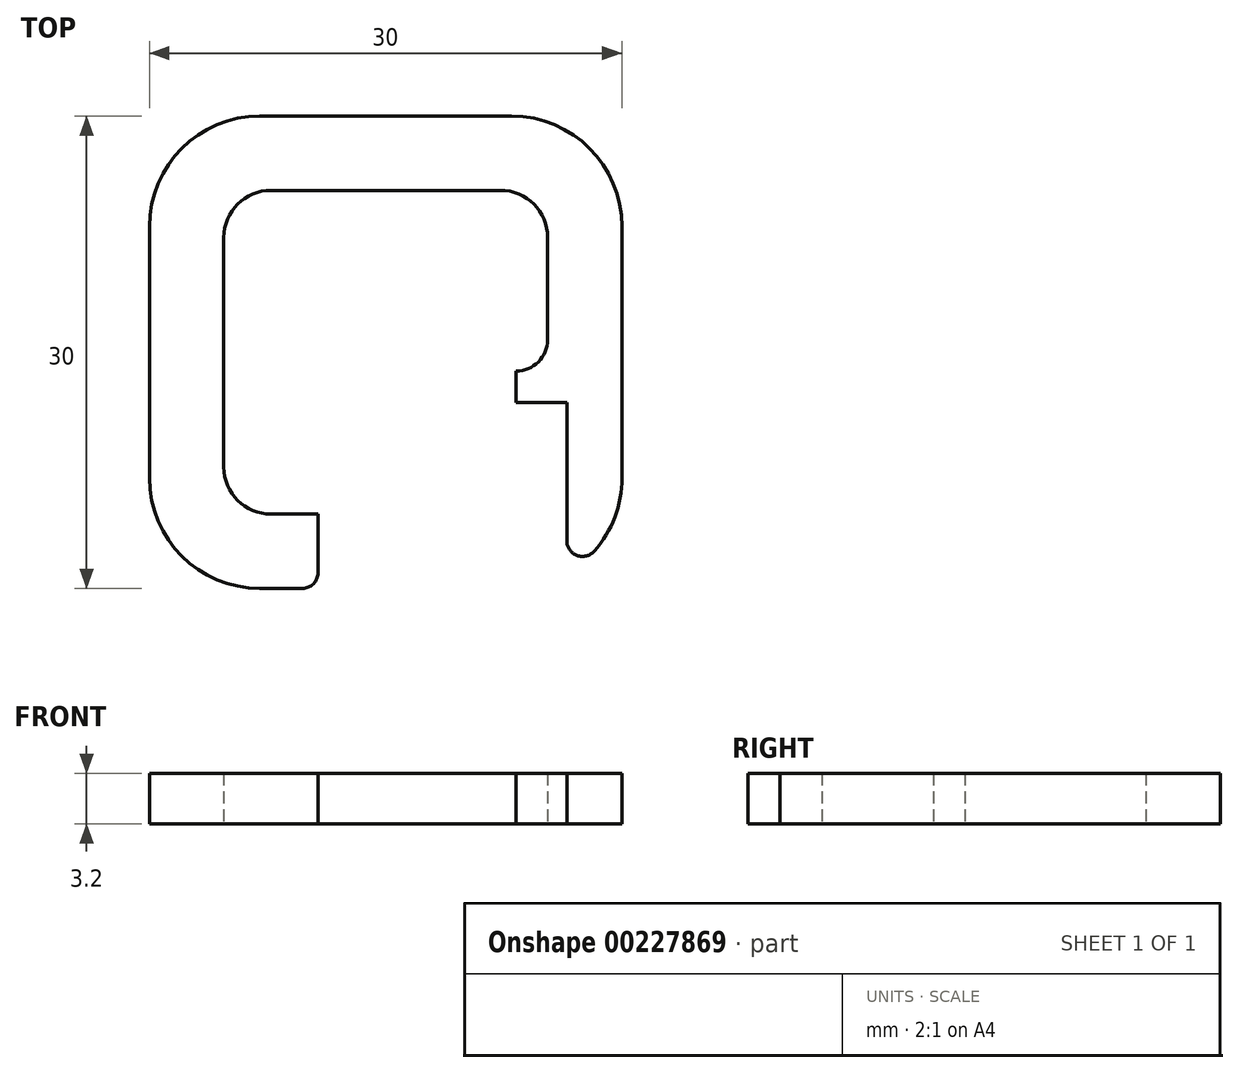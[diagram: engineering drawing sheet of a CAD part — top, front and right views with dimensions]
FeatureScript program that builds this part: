
annotation { "Feature Type Name" : "Feature", "Feature Type Description" : "" }
export const myFeature = defineFeature(function(context is Context, id is Id, definition is map)
    precondition{}
    {
        {
            var Q0;
            Q0=qCreatedBy(makeId("Top.planeOp"),FACE);
            var sketch = newSketch(context, id + "F0", { "sketchPlane" : qUnion([Q0])});
            skLineSegment(sketch, "E0.bottom", {"start": v(8, 15) * mm, "end": v(-8, 15) * mm});
            skLineSegment(sketch, "E0.left", {"start": v(15, 8) * mm, "end": v(15, -8) * mm});
            skLineSegment(sketch, "E0.right", {"start": v(-15, 8) * mm, "end": v(-15, -8) * mm});
            skPoint(sketch, "E1.visualSharp", {"position": v(-15, 15) * mm});
            skArc(sketch, "E1.filletArc", {"start": v(-8, 15) * mm, "mid": v(-12.95, 12.95) * mm, "end": v(-15, 8) * mm});
            skPoint(sketch, "E2.visualSharp", {"position": v(15, 15) * mm});
            skArc(sketch, "E2.filletArc", {"start": v(15, 8) * mm, "mid": v(12.95, 12.95) * mm, "end": v(8, 15) * mm});
            skPoint(sketch, "E3.visualSharp", {"position": v(15, -15) * mm});
            skArc(sketch, "E3.filletArc", {"start": v(13.25, -12.63) * mm, "mid": v(14.55, -10.47) * mm, "end": v(15, -8) * mm});
            skPoint(sketch, "E4.visualSharp", {"position": v(-15, -15) * mm});
            skArc(sketch, "E4.filletArc", {"start": v(-15, -8) * mm, "mid": v(-12.95, -12.95) * mm, "end": v(-8, -15) * mm});
            skLineSegment(sketch, "E5.left", {"start": v(-4.3, -14) * mm, "end": v(-4.3, -10.28) * mm});
            skLineSegment(sketch, "E5.right", {"start": v(11.5, -11.97) * mm, "end": v(11.5, -3.2) * mm});
            skLineSegment(sketch, "E6", {"start": v(-8, -15) * mm, "end": v(-5.3, -15) * mm});
            skPoint(sketch, "E7.visualSharp", {"position": v(-4.3, -15) * mm});
            skArc(sketch, "E7.filletArc", {"start": v(-5.3, -15) * mm, "mid": v(-4.6, -14.7) * mm, "end": v(-4.3, -14) * mm});
            skPoint(sketch, "E8.orphan", {"position": v(11.5, -15) * mm});
            skPoint(sketch, "E9.visualSharp", {"position": v(11.5, -14.06) * mm});
            skArc(sketch, "E9.filletArc", {"start": v(11.5, -11.97) * mm, "mid": v(12.15, -12.9) * mm, "end": v(13.25, -12.63) * mm});
            skLineSegment(sketch, "E10.top", {"start": v(7.28, 10.28) * mm, "end": v(-7.28, 10.28) * mm});
            skLineSegment(sketch, "E10.left", {"start": v(10.28, 0.8) * mm, "end": v(10.28, 7.28) * mm});
            skLineSegment(sketch, "E10.right", {"start": v(-10.28, -7.28) * mm, "end": v(-10.28, 7.28) * mm});
            skPoint(sketch, "E11.visualSharp", {"position": v(-10.28, 10.28) * mm});
            skArc(sketch, "E11.filletArc", {"start": v(-7.28, 10.28) * mm, "mid": v(-9.4, 9.4) * mm, "end": v(-10.28, 7.28) * mm});
            skPoint(sketch, "E12.visualSharp", {"position": v(10.28, 10.28) * mm});
            skArc(sketch, "E12.filletArc", {"start": v(10.28, 7.28) * mm, "mid": v(9.4, 9.4) * mm, "end": v(7.28, 10.28) * mm});
            skPoint(sketch, "E13.visualSharp", {"position": v(-10.28, -10.28) * mm});
            skArc(sketch, "E13.filletArc", {"start": v(-10.28, -7.28) * mm, "mid": v(-9.4, -9.4) * mm, "end": v(-7.28, -10.28) * mm});
            skLineSegment(sketch, "E14.trimOffspring", {"start": v(-4.3, -10.28) * mm, "end": v(-7.28, -10.28) * mm});
            skLineSegment(sketch, "E15.trimOffspring", {"start": v(10.28, -3.2) * mm, "end": v(11.5, -3.2) * mm});
            skLineSegment(sketch, "E16", {"start": v(8.28, -1.2) * mm, "end": v(8.28, -1.2) * mm});
            skLineSegment(sketch, "E17", {"start": v(8.28, -1.2) * mm, "end": v(8.28, -3.2) * mm});
            skLineSegment(sketch, "E18", {"start": v(8.28, -3.2) * mm, "end": v(10.28, -3.2) * mm});
            skPoint(sketch, "E19.visualSharp", {"position": v(10.28, -1.2) * mm});
            skArc(sketch, "E19.filletArc", {"start": v(8.28, -1.2) * mm, "mid": v(9.7, -0.61) * mm, "end": v(10.28, 0.8) * mm});
            skSolve(sketch);
        }
        {
            var Q0;
            Q0=makeQuery(id+"F0.imprint","IMPRINT",FACE,{"disambiguationData":[TD([[makeQuery(id+"F0.imprint","IMPRINT",EDGE,{"derivedFrom":sQuery(id+"F0.wireOp",EDGE,"E0.bottom")}),1.0]])]});
            extrude(context, id + "F1", {"entities" : qUnion([Q0]), "depth" : 3.2 * mm});
        }
    });
